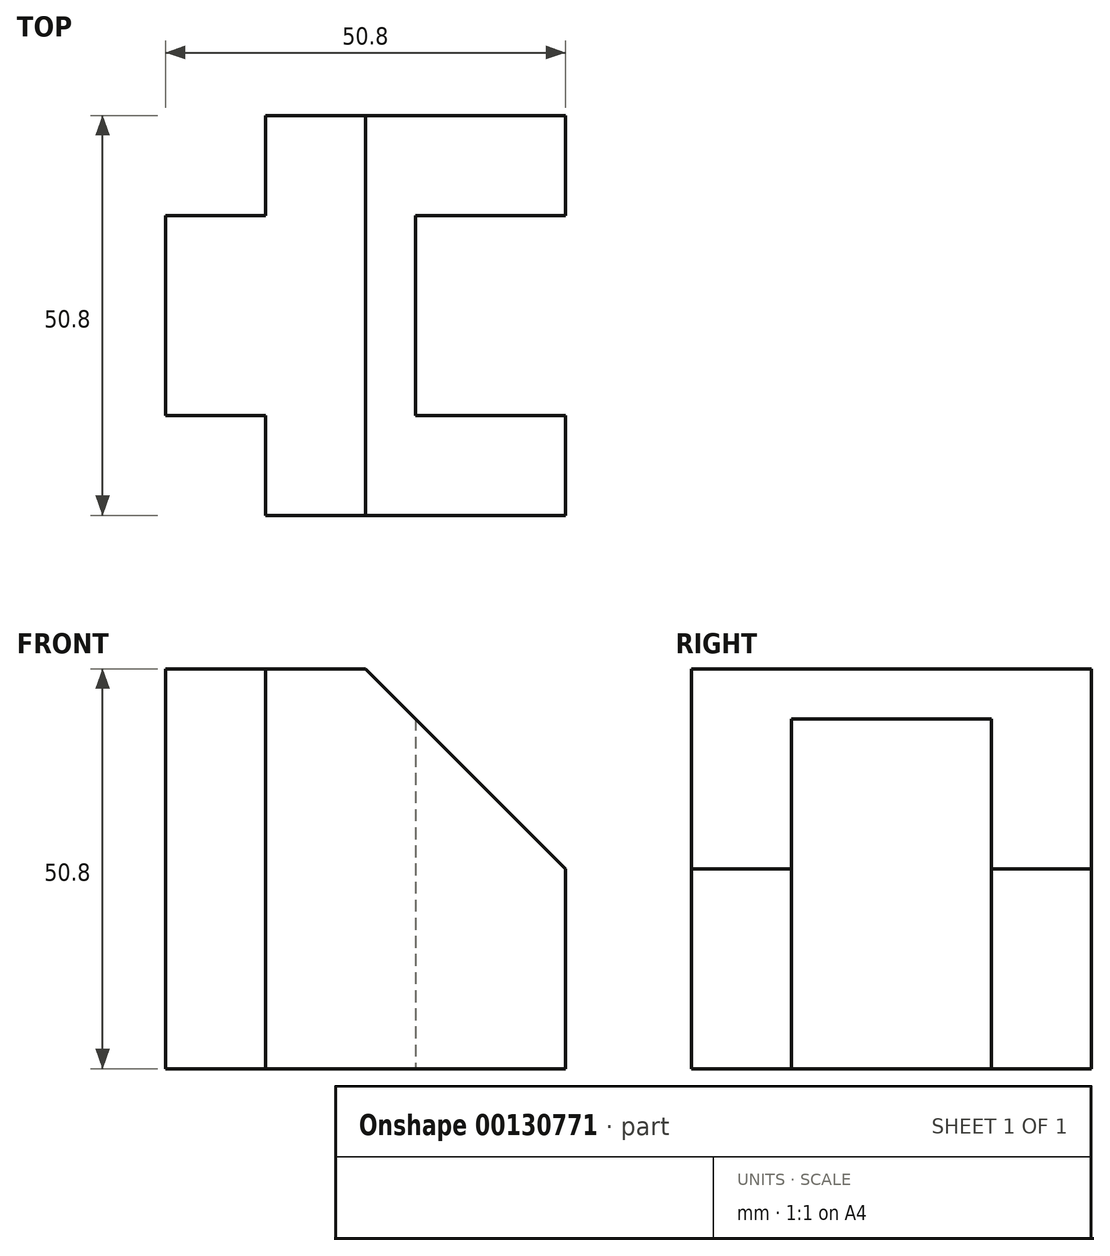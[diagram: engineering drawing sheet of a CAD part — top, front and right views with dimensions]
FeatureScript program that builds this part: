
annotation { "Feature Type Name" : "Feature", "Feature Type Description" : "" }
export const myFeature = defineFeature(function(context is Context, id is Id, definition is map)
    precondition{}
    {
        {
            var Q0;
            Q0=qCreatedBy(makeId("Top.planeOp"),FACE);
            var sketch = newSketch(context, id + "F0", { "sketchPlane" : qUnion([Q0])});
            skLineSegment(sketch, "E0", {"start": v(0, 0) * mm, "end": v(12.7, 0) * mm});
            skLineSegment(sketch, "E1", {"start": v(12.7, 0) * mm, "end": v(12.7, -12.7) * mm});
            skLineSegment(sketch, "E2", {"start": v(12.7, -12.7) * mm, "end": v(50.8, -12.7) * mm});
            skLineSegment(sketch, "E3", {"start": v(50.8, -12.7) * mm, "end": v(50.8, 0) * mm});
            skLineSegment(sketch, "E4", {"start": v(50.8, 0) * mm, "end": v(31.75, 0) * mm});
            skLineSegment(sketch, "E5", {"start": v(31.75, 0) * mm, "end": v(31.75, 25.4) * mm});
            skLineSegment(sketch, "E6", {"start": v(31.75, 25.4) * mm, "end": v(50.8, 25.4) * mm});
            skLineSegment(sketch, "E7", {"start": v(50.8, 25.4) * mm, "end": v(50.8, 38.1) * mm});
            skLineSegment(sketch, "E8", {"start": v(50.8, 38.1) * mm, "end": v(12.7, 38.1) * mm});
            skLineSegment(sketch, "E9", {"start": v(12.7, 38.1) * mm, "end": v(12.7, 25.4) * mm});
            skLineSegment(sketch, "E10", {"start": v(12.7, 25.4) * mm, "end": v(0, 25.4) * mm});
            skLineSegment(sketch, "E11", {"start": v(0, 25.4) * mm, "end": v(0, 0) * mm});
            skLineSegment(sketch, "E12", {"start": v(25.4, 38.1) * mm, "end": v(25.4, -12.7) * mm});
            skSolve(sketch);
        }
        {
            var Q0;
            Q0 = qSketchRegion(id + "F0", true);
            extrude(context, id + "F1", {"entities" : qUnion([Q0]), "depth" : 50.8 * mm});
        }
        {
            var Q0;
            Q0=qCreatedBy(makeId("Front.planeOp"),FACE);
            var sketch = newSketch(context, id + "F2", { "sketchPlane" : qUnion([Q0])});
            skLineSegment(sketch, "E13", {"start": v(25.4, 50.8) * mm, "end": v(50.8, 25.4) * mm});
            skLineSegment(sketch, "E14", {"start": v(25.4, 50.8) * mm, "end": v(50.8, 50.8) * mm});
            skLineSegment(sketch, "E15", {"start": v(50.8, 50.8) * mm, "end": v(50.8, 25.4) * mm});
            skSolve(sketch);
        }
        {
            var Q0;
            Q0 = qSketchRegion(id + "F2", true);
            extrude(context, id + "F3", {"entities" : qUnion([Q0]), "operationType" : NewBodyOperationType.REMOVE, "endBound" : BoundingType.THROUGH_ALL, "oppositeDirection" : true, "depth" : 25.4 * mm, "hasSecondDirection" : true, "secondDirectionBound" : SecondDirectionBoundingType.THROUGH_ALL, "secondDirectionOppositeDirection" : false, "secondDirectionDepth" : 25.4 * mm});
        }
    });
